# Revit family: BTB-Grop
name_source: partatom
category: Structural Foundations
units: mm (PartAtom-declared; Revit-internal decimal feet)

## family parameters
Always vertical = Yes
Cap = No
Cut with Voids When Loaded = Yes
Host = Floor
Material for Model Behavior = Other
Shared = No

## types (2) — shared parameters
Hole_Length = 2500 mm  [stored 8.2021 ft]
Slab Outline Offset = 200 mm  [stored 0.656168 ft]
Slab_Thickness = 300 mm  [stored 0.984252 ft]
Wall_Thickness = 250 mm  [stored 0.82021 ft]
zero-valued in all types: Hole_Depth, Top_Offset

## per-type parameters (varying)
| type | Depth | Hole_Width | Shaft_Height | Width |
| Grop, 2000x2500, -1100 | 1100 mm | 2000 mm  [stored 6.56168 ft] | 7000 mm  [stored 22.9659 ft] | 2500 mm  [stored 8.2021 ft] |
| Elgrop, 800x2500, -600 | 600 mm | 800 mm  [stored 2.62467 ft] | 1500 mm  [stored 4.92126 ft] | 1300 mm  [stored 4.26509 ft] |

note: [stored X ft] marks values corroborated as IEEE doubles in the binary element streams (Revit-internal decimal feet)

## geometry (parser evidence)
native form markers: Blend x3, Sweep x6
no freeform markers — native parametric forms only
